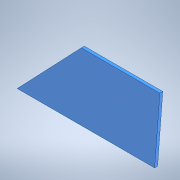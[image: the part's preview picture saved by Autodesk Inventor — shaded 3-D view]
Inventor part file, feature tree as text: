
AUTODESK INVENTOR PART (.ipt)
format: ipt  version: 2020 (Build 240168000, 168)  size: 95,744 bytes
history: native  units: mm
features: extrude x1, sketch x1
ambient origin geometry x8: Origin, YZ Plane, XZ Plane, XY Plane, X Axis, Y Axis, Z Axis, Center Point
bodies: Solid1 (feature_tree)
feature tree (2):
  extrude  "Extrusion1"  Depth=3.0mm
  sketch  "Sketch1"  dims[d0=140.0mm d1=94.7mm d2=8.098328mm d3=80.0mm d4=3.0mm d5=0.0mm]
